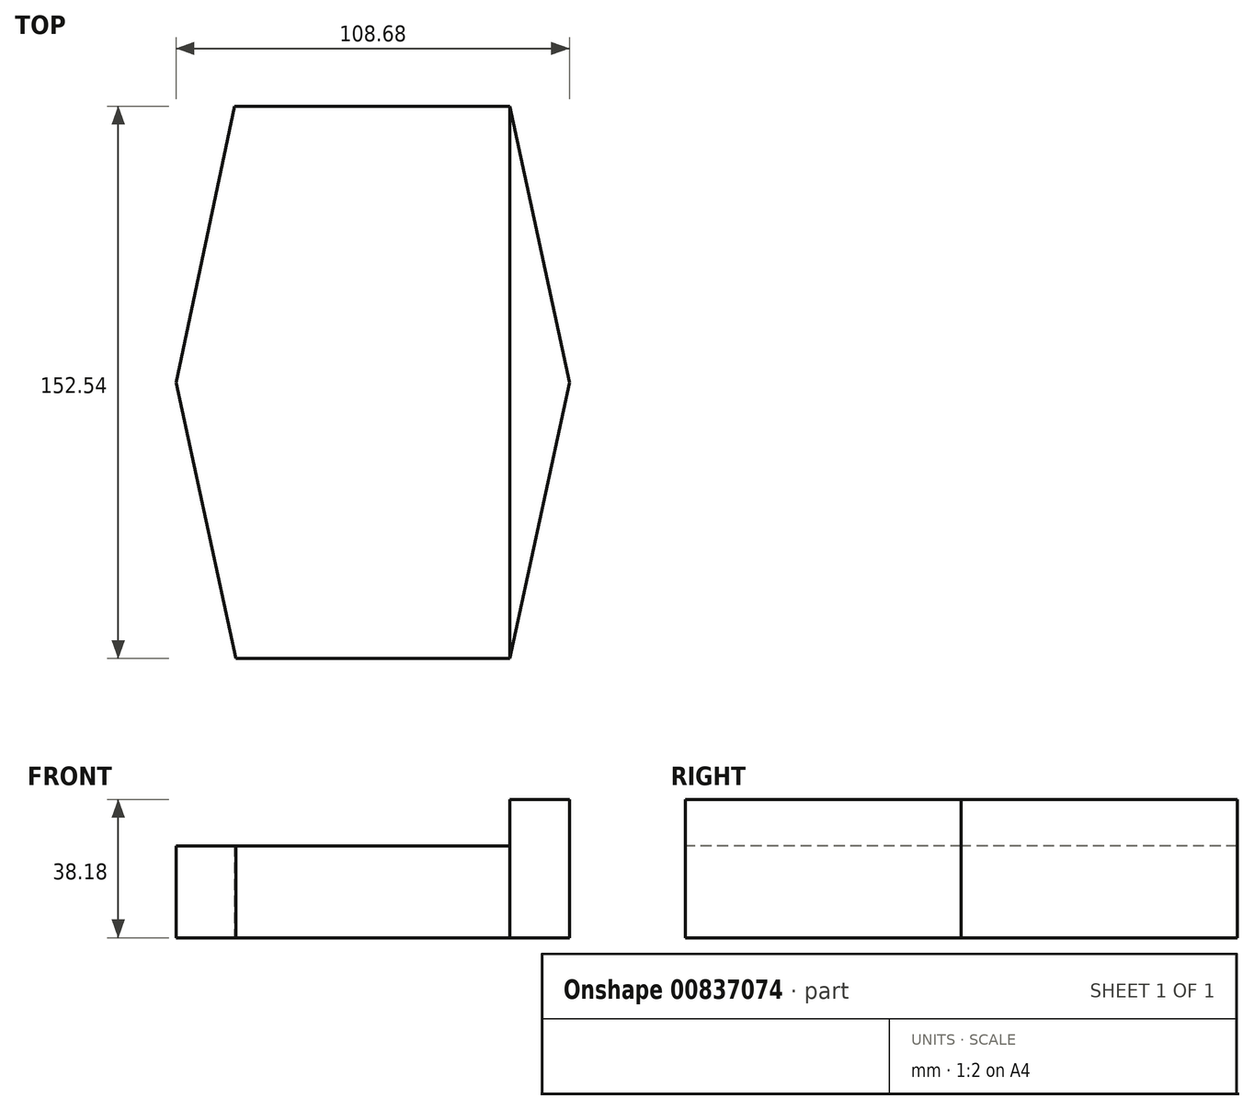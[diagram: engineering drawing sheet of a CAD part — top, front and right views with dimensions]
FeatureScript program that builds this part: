
annotation { "Feature Type Name" : "Feature", "Feature Type Description" : "" }
export const myFeature = defineFeature(function(context is Context, id is Id, definition is map)
    precondition{}
    {
        {
            var Q0;
            Q0=qCreatedBy(makeId("Top.planeOp"),FACE);
            var sketch = newSketch(context, id + "F0", { "sketchPlane" : qUnion([Q0])});
            skLineSegment(sketch, "E0", {"start": v(0, 76.29) * mm, "end": v(-76, 76.29) * mm});
            skLineSegment(sketch, "E1", {"start": v(-76, 76.29) * mm, "end": v(-92.15, 0) * mm});
            skLineSegment(sketch, "E2", {"start": v(-92.15, 0) * mm, "end": v(-75.6, -76.25) * mm});
            skLineSegment(sketch, "E3", {"start": v(-75.6, -76.25) * mm, "end": v(0, -76.25) * mm});
            skLineSegment(sketch, "E4", {"start": v(0, -76.25) * mm, "end": v(16.53, 0) * mm});
            skLineSegment(sketch, "E5", {"start": v(16.53, 0) * mm, "end": v(0, 76.29) * mm});
            skSolve(sketch);
        }
        {
            var Q0;
            Q0=makeQuery(id+"F0.imprint","IMPRINT",FACE,{"disambiguationData":[TD([[makeQuery(id+"F0.imprint","IMPRINT",EDGE,{"derivedFrom":sQuery(id+"F0.wireOp",EDGE,"E0")}),1.0]])]});
            extrude(context, id + "F1", {"entities" : qUnion([Q0]), "depth" : 25.4 * mm, "offsetDistance" : 25.4 * mm});
        }
        {
            var Q0;
            Q0=makeQuery(id+"F1.opExtrude","CAP_FACE",FACE,{"disambiguationData":[OSD([sQuery(id+"F0.wireOp",EDGE,"E0"),sQuery(id+"F0.wireOp",EDGE,"E1"),sQuery(id+"F0.wireOp",EDGE,"E2"),sQuery(id+"F0.wireOp",EDGE,"E3"),sQuery(id+"F0.wireOp",EDGE,"E4"),sQuery(id+"F0.wireOp",EDGE,"E5")])],"isStart":false});
            var sketch = newSketch(context, id + "F2", { "sketchPlane" : qUnion([Q0])});
            skLineSegment(sketch, "E6", {"start": v(0, -76.25) * mm, "end": v(0, 0) * mm});
            skLineSegment(sketch, "E7", {"start": v(0, 0) * mm, "end": v(0, 76.29) * mm});
            skSolve(sketch);
        }
        {
            var Q0;
            Q0=makeQuery(id+"F2.imprint","IMPRINT",FACE,{"disambiguationData":[TD([[makeQuery(id+"F2.imprint","IMPRINT",EDGE,{"derivedFrom":sQuery(id+"F2.wireOp",EDGE,"E6")}),-1.0]])]});
            extrude(context, id + "F3", {"entities" : qUnion([Q0]), "operationType" : NewBodyOperationType.ADD, "depth" : 12.78 * mm, "offsetDistance" : 25.4 * mm});
        }
    });
